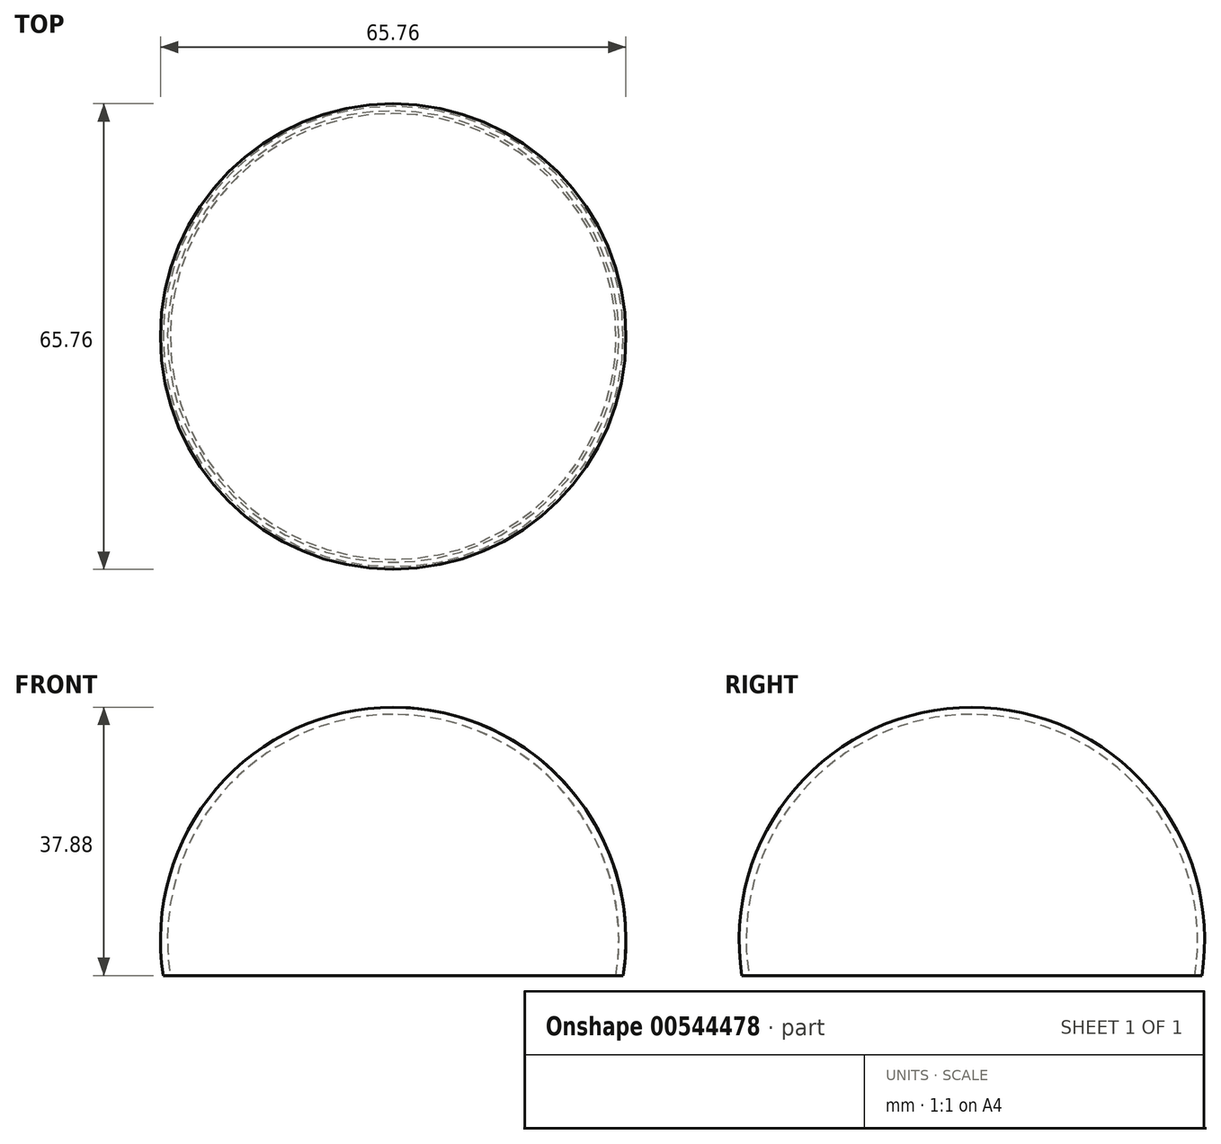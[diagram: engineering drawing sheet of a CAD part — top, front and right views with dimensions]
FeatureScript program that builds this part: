
annotation { "Feature Type Name" : "Feature", "Feature Type Description" : "" }
export const myFeature = defineFeature(function(context is Context, id is Id, definition is map)
    precondition{}
    {
        {
            var Q0;
            Q0=qCreatedBy(makeId("Front.planeOp"),FACE);
            var sketch = newSketch(context, id + "F0", { "sketchPlane" : qUnion([Q0])});
            skCircle(sketch, "E0", {"center": v(0, 5) * mm, "radius": 32.88 * mm});
            skLineSegment(sketch, "E1", {"start": v(-32.5, 0) * mm, "end": v(32.5, 0) * mm});
            skCircle(sketch, "E2.0", {"center": v(0, 5) * mm, "radius": 31.88 * mm});
            skLineSegment(sketch, "E3", {"start": v(0, 37.88) * mm, "end": v(0, 36.88) * mm});
            skSolve(sketch);
        }
        {
            var Q0;
            {var subQ3=sQuery(id+"F0.wireOp",EDGE,"E3");Q0=makeQuery(id+"F0.imprint","IMPRINT",FACE,{"disambiguationData":[TD([[makeQuery(id+"F0.imprint","IMPRINT",EDGE,{"derivedFrom":subQ3}),1.0]])]});}
            var Q1;
            Q1=sQuery(id+"F0.wireOp",EDGE,"E3");
            revolve(context, id + "F1", {"entities" : qUnion([Q0]), "axis" : qUnion([Q1]), "revolveType" : RevolveType.FULL});
        }
    });
